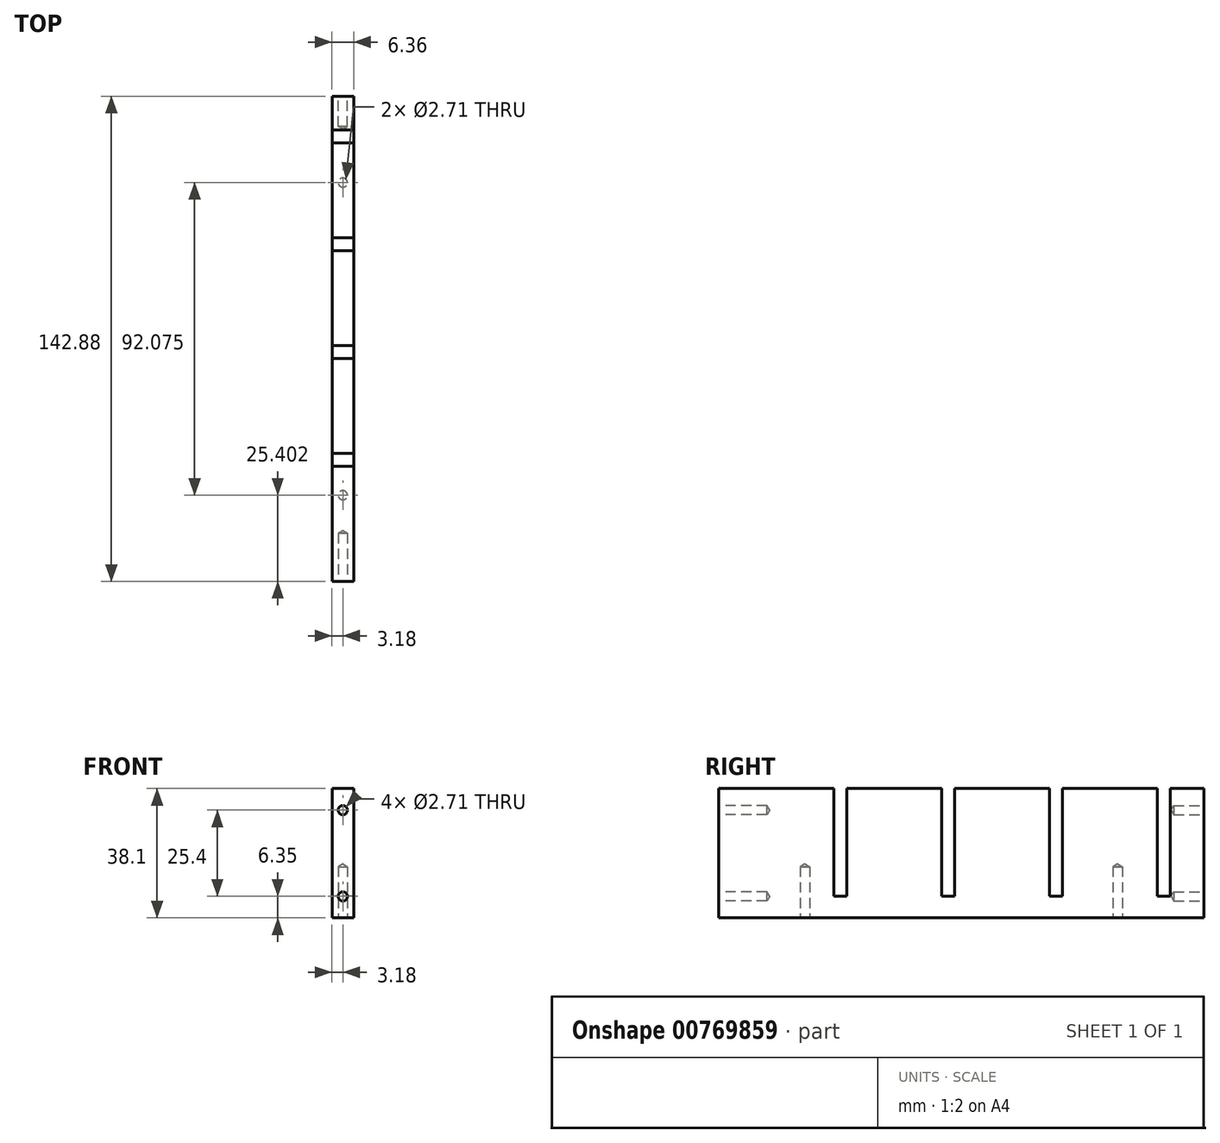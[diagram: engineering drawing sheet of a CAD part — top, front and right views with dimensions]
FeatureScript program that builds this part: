
annotation { "Feature Type Name" : "Feature", "Feature Type Description" : "" }
export const myFeature = defineFeature(function(context is Context, id is Id, definition is map)
    precondition{}
    {
        {
            var Q0;
            Q0=qCreatedBy(makeId("Top.planeOp"),FACE);
            var sketch = newSketch(context, id + "F0", { "sketchPlane" : qUnion([Q0])});
            skLineSegment(sketch, "E0.bottom", {"start": v(-3.17, 71.44) * mm, "end": v(3.18, 71.44) * mm});
            skLineSegment(sketch, "E0.top", {"start": v(-3.18, -71.44) * mm, "end": v(3.17, -71.44) * mm});
            skLineSegment(sketch, "E0.left", {"start": v(-3.17, 71.44) * mm, "end": v(-3.18, -71.44) * mm});
            skLineSegment(sketch, "E0.right", {"start": v(3.18, 71.44) * mm, "end": v(3.17, -71.44) * mm});
            skLineSegment(sketch, "E1", {"start": v(3.18, 71.44) * mm, "end": v(-3.18, -71.44) * mm, "construction": true});
            skSolve(sketch);
        }
        {
            var Q0;
            Q0=qSketchRegion(id+"F0",true);
            extrude(context, id + "F1", {"entities" : qUnion([Q0]), "depth" : 38.1 * mm, "offsetDistance" : 25.4 * mm});
        }
        {
            var Q0;
            Q0=makeQuery(id+"F1.opExtrude","SWEPT_FACE",FACE,{"disambiguationData":[OSD([sQuery(id+"F0.wireOp",EDGE,"E0.left")])]});
            var sketch = newSketch(context, id + "F2", { "sketchPlane" : qUnion([Q0])});
            skLineSegment(sketch, "E2", {"start": v(-71.44, 6.35) * mm, "end": v(71.44, 6.35) * mm, "construction": true});
            skLineSegment(sketch, "E3.bottom", {"start": v(-61.6, 38.1) * mm, "end": v(-57.79, 38.1) * mm});
            skLineSegment(sketch, "E3.top", {"start": v(-61.6, 6.35) * mm, "end": v(-57.79, 6.35) * mm});
            skLineSegment(sketch, "E3.left", {"start": v(-61.6, 38.1) * mm, "end": v(-61.6, 6.35) * mm});
            skLineSegment(sketch, "E3.right", {"start": v(-57.79, 38.1) * mm, "end": v(-57.78, 6.35) * mm});
            skLineSegment(sketch, "E4.bottom", {"start": v(-29.84, 38.1) * mm, "end": v(-26.04, 38.1) * mm});
            skLineSegment(sketch, "E4.top", {"start": v(-29.84, 6.35) * mm, "end": v(-26.04, 6.35) * mm});
            skLineSegment(sketch, "E4.left", {"start": v(-29.84, 38.1) * mm, "end": v(-29.84, 6.35) * mm});
            skLineSegment(sketch, "E4.right", {"start": v(-26.04, 38.1) * mm, "end": v(-26.04, 6.35) * mm});
            skLineSegment(sketch, "E5.bottom", {"start": v(1.9, 38.1) * mm, "end": v(5.71, 38.1) * mm});
            skLineSegment(sketch, "E5.top", {"start": v(1.9, 6.35) * mm, "end": v(5.71, 6.35) * mm});
            skLineSegment(sketch, "E5.left", {"start": v(1.9, 38.1) * mm, "end": v(1.9, 6.35) * mm});
            skLineSegment(sketch, "E5.right", {"start": v(5.71, 38.1) * mm, "end": v(5.72, 6.35) * mm});
            skLineSegment(sketch, "E6.bottom", {"start": v(33.66, 38.1) * mm, "end": v(37.46, 38.1) * mm});
            skLineSegment(sketch, "E6.top", {"start": v(33.66, 6.35) * mm, "end": v(37.46, 6.35) * mm});
            skLineSegment(sketch, "E6.left", {"start": v(33.66, 38.1) * mm, "end": v(33.66, 6.35) * mm});
            skLineSegment(sketch, "E6.right", {"start": v(37.46, 38.1) * mm, "end": v(37.46, 6.35) * mm});
            skPoint(sketch, "E7", {"position": v(-59.69, 6.35) * mm});
            skPoint(sketch, "E8", {"position": v(-27.94, 6.35) * mm});
            skPoint(sketch, "E9", {"position": v(3.81, 6.35) * mm});
            skPoint(sketch, "E10", {"position": v(35.56, 6.35) * mm});
            skSolve(sketch);
        }
        {
            var Q0;
            Q0 = qSketchRegion(id + "F2", true);
            extrude(context, id + "F3", {"entities" : qUnion([Q0]), "operationType" : NewBodyOperationType.REMOVE, "endBound" : BoundingType.THROUGH_ALL, "oppositeDirection" : true, "depth" : 25.4 * mm, "offsetDistance" : 25.4 * mm});
        }
        {
            var Q0;
            Q0=makeQuery(id+"F1.opExtrude","CAP_FACE",FACE,{"disambiguationData":[OSD([sQuery(id+"F0.wireOp",EDGE,"E0.bottom"),sQuery(id+"F0.wireOp",EDGE,"E0.top"),sQuery(id+"F0.wireOp",EDGE,"E0.left"),sQuery(id+"F0.wireOp",EDGE,"E0.right")])],"isStart":true});
            var sketch = newSketch(context, id + "F4", { "sketchPlane" : qUnion([Q0])});
            skLineSegment(sketch, "E11", {"start": v(0, 71.44) * mm, "end": v(0, -71.44) * mm, "construction": true});
            skPoint(sketch, "E12", {"position": v(0, 46.04) * mm});
            skPoint(sketch, "E13", {"position": v(0, -46.04) * mm});
            skSolve(sketch);
        }
        {
            var Q0;
            Q0=sQuery(id+"F4.wireOp",VERTEX,"E12");
            var Q1;
            Q1=sQuery(id+"F4.wireOp",VERTEX,"E13");
            var Q2;
            Q2=makeQuery(id+"F1.opExtrude","SWEPT_BODY",BODY,{"disambiguationData":[OSD([sQuery(id+"F0.wireOp",EDGE,"E0.bottom"),sQuery(id+"F0.wireOp",EDGE,"E0.top"),sQuery(id+"F0.wireOp",EDGE,"E0.left"),sQuery(id+"F0.wireOp",EDGE,"E0.right")])]});
            hole(context, id + "F5", {"style" : HoleStyle.SIMPLE, "endStyle" : HoleEndStyle.BLIND, "standardTappedOrClearance" : lookupTablePath({ "standard" : "ANSI", "engagement" : "75%", "pitch" : "32 tpi", "size" : "#6", "type" : "Tapped" }), "standardBlindInLast" : lookupTablePath({ "standard" : "ANSI", "engagement" : "75%", "pitch" : "32 tpi", "size" : "#6", "type" : "Tapped" }), "holeDiameter" : 2.7 * mm, "majorDiameter" : 3.5 * mm, "showTappedDepth" : true, "holeDepth" : 15.1 * mm, "tappedDepth" : 12.7 * mm, "tapClearance" : 3, "locations" : qUnion([Q0, Q1]), "scope" : qUnion([Q2])});
        }
        {
            var Q0;
            Q0=makeQuery(id+"F1.opExtrude","SWEPT_FACE",FACE,{"disambiguationData":[OSD([sQuery(id+"F0.wireOp",EDGE,"E0.top")])]});
            var sketch = newSketch(context, id + "F6", { "sketchPlane" : qUnion([Q0])});
            skLineSegment(sketch, "E14", {"start": v(0, 38.1) * mm, "end": v(0, 0) * mm, "construction": true});
            skPoint(sketch, "E15", {"position": v(0, 31.75) * mm});
            skPoint(sketch, "E16", {"position": v(0, 19.05) * mm});
            skPoint(sketch, "E17", {"position": v(0, 6.35) * mm});
            skSolve(sketch);
        }
        {
            var Q0;
            Q0=makeQuery(id+"F1.opExtrude","SWEPT_FACE",FACE,{"disambiguationData":[OSD([sQuery(id+"F0.wireOp",EDGE,"E0.bottom")])]});
            var sketch = newSketch(context, id + "F7", { "sketchPlane" : qUnion([Q0])});
            skLineSegment(sketch, "E18", {"start": v(0, 38.1) * mm, "end": v(0, 0) * mm});
            skPoint(sketch, "E19", {"position": v(0, 6.35) * mm});
            skPoint(sketch, "E20", {"position": v(0, 19.05) * mm});
            skPoint(sketch, "E21", {"position": v(0, 31.75) * mm});
            skSolve(sketch);
        }
        {
            var Q0;
            Q0=sQuery(id+"F6.wireOp",VERTEX,"E15");
            var Q1;
            Q1=sQuery(id+"F6.wireOp",VERTEX,"E17");
            var Q2;
            Q2=makeQuery(id+"F1.opExtrude","SWEPT_BODY",BODY,{"disambiguationData":[OSD([sQuery(id+"F0.wireOp",EDGE,"E0.bottom"),sQuery(id+"F0.wireOp",EDGE,"E0.top"),sQuery(id+"F0.wireOp",EDGE,"E0.left"),sQuery(id+"F0.wireOp",EDGE,"E0.right")])]});
            hole(context, id + "F8", {"style" : HoleStyle.SIMPLE, "endStyle" : HoleEndStyle.BLIND, "standardTappedOrClearance" : lookupTablePath({ "standard" : "ANSI", "engagement" : "75%", "pitch" : "32 tpi", "size" : "#6", "type" : "Tapped" }), "standardBlindInLast" : lookupTablePath({ "standard" : "ANSI", "engagement" : "75%", "pitch" : "32 tpi", "size" : "#6", "type" : "Tapped" }), "holeDiameter" : 2.7 * mm, "majorDiameter" : 3.5 * mm, "showTappedDepth" : true, "holeDepth" : 14.22 * mm, "tappedDepth" : 11.84 * mm, "tapClearance" : 3, "locations" : qUnion([Q0, Q1]), "scope" : qUnion([Q2])});
        }
        {
            var Q0;
            Q0=sQuery(id+"F7.wireOp",VERTEX,"E21");
            var Q1;
            Q1=sQuery(id+"F7.wireOp",VERTEX,"E19");
            var Q2;
            Q2=makeQuery(id+"F1.opExtrude","SWEPT_BODY",BODY,{"disambiguationData":[OSD([sQuery(id+"F0.wireOp",EDGE,"E0.bottom"),sQuery(id+"F0.wireOp",EDGE,"E0.top"),sQuery(id+"F0.wireOp",EDGE,"E0.left"),sQuery(id+"F0.wireOp",EDGE,"E0.right")])]});
            hole(context, id + "F9", {"style" : HoleStyle.SIMPLE, "endStyle" : HoleEndStyle.BLIND, "standardTappedOrClearance" : lookupTablePath({ "standard" : "ANSI", "engagement" : "75%", "pitch" : "32 tpi", "size" : "#6", "type" : "Tapped" }), "standardBlindInLast" : lookupTablePath({ "fit" : "Free", "standard" : "ANSI", "engagement" : "75%", "pitch" : "32 tpi", "size" : "#6", "type" : "Clearance & tapped" }), "holeDiameter" : 2.7 * mm, "majorDiameter" : 3.5 * mm, "showTappedDepth" : true, "holeDepth" : 8.9 * mm, "tappedDepth" : 6.5 * mm, "tapClearance" : 3, "locations" : qUnion([Q0, Q1]), "scope" : qUnion([Q2])});
        }
    });
